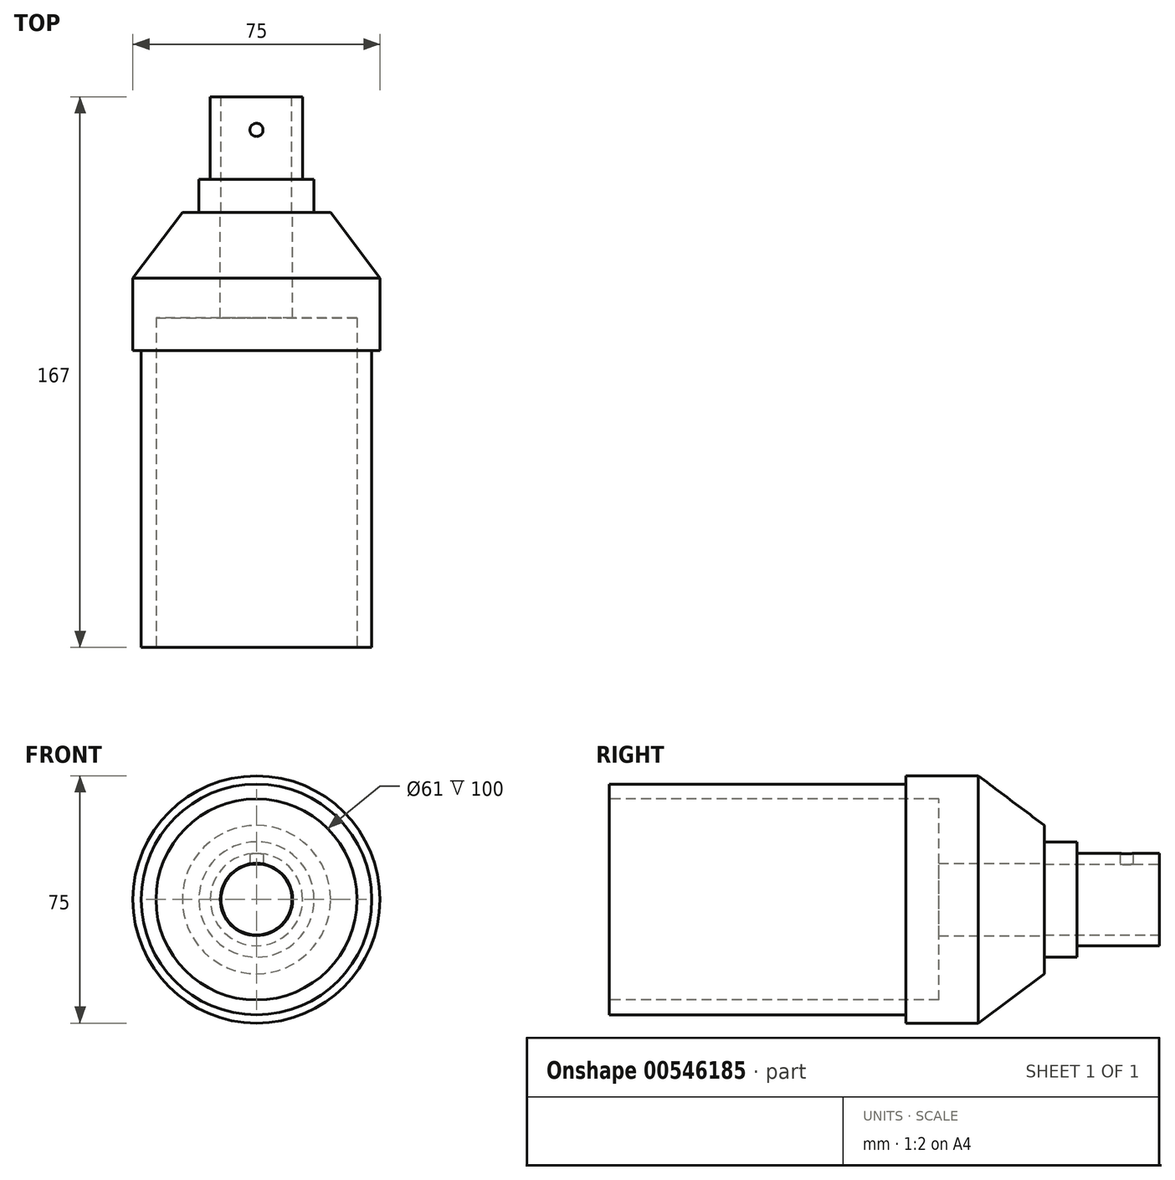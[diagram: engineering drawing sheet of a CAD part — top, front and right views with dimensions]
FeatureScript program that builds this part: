
annotation { "Feature Type Name" : "Feature", "Feature Type Description" : "" }
export const myFeature = defineFeature(function(context is Context, id is Id, definition is map)
    precondition{}
    {
        {
            var Q0;
            Q0=qCreatedBy(makeId("Front.planeOp"),FACE);
            var sketch = newSketch(context, id + "F0", { "sketchPlane" : qUnion([Q0])});
            skCircle(sketch, "E0", {"center": v(0, 0) * mm, "radius": 11 * mm});
            skCircle(sketch, "E1", {"center": v(0, 0) * mm, "radius": 37.5 * mm});
            skSolve(sketch);
        }
        {
            var Q0;
            Q0 = qSketchRegion(id + "F0", true);
            extrude(context, id + "F1", {"entities" : qUnion([Q0]), "depth" : 22 * mm, "offsetDistance" : 25 * mm});
        }
        {
            var Q0;
            Q0=makeQuery(id+"F1.opExtrude","CAP_FACE",FACE,{"disambiguationData":[OSD([sQuery(id+"F0.wireOp",EDGE,"E0"),sQuery(id+"F0.wireOp",EDGE,"E1")])],"isStart":false});
            var sketch = newSketch(context, id + "F2", { "sketchPlane" : qUnion([Q0])});
            skCircle(sketch, "E2", {"center": v(0, 0) * mm, "radius": 35 * mm});
            skSolve(sketch);
        }
        {
            var Q0;
            Q0 = qSketchRegion(id + "F2", true);
            extrude(context, id + "F3", {"entities" : qUnion([Q0]), "operationType" : NewBodyOperationType.ADD, "depth" : 90 * mm, "offsetDistance" : 25 * mm});
        }
        {
            var Q0;
            Q0=makeQuery(id+"F3.opExtrude","CAP_FACE",FACE,{"disambiguationData":[OSD([sQuery(id+"F2.wireOp",EDGE,"E2")])],"isStart":false});
            var sketch = newSketch(context, id + "F4", { "sketchPlane" : qUnion([Q0])});
            skCircle(sketch, "E3", {"center": v(0, 0) * mm, "radius": 30.5 * mm});
            skSolve(sketch);
        }
        {
            var Q0;
            Q0 = qSketchRegion(id + "F4", true);
            extrude(context, id + "F5", {"entities" : qUnion([Q0]), "operationType" : NewBodyOperationType.REMOVE, "oppositeDirection" : true, "depth" : 100 * mm, "offsetDistance" : 25 * mm});
        }
        {
            var Q0;
            Q0=makeQuery(id+"F1.opExtrude","CAP_FACE",FACE,{"disambiguationData":[OSD([sQuery(id+"F0.wireOp",EDGE,"E0"),sQuery(id+"F0.wireOp",EDGE,"E1")])],"isStart":true});
            var sketch = newSketch(context, id + "F6", { "sketchPlane" : qUnion([Q0])});
            skSolve(sketch);
        }
        {
            var Q0;
            Q0 = qSketchRegion(id + "F6", true);
            var Q1;
            Q1=makeQuery(id+"F6.imprint","IMPRINT",FACE,{"disambiguationData":[TD([[makeQuery(id+"F6.imprint","IMPRINT",EDGE,{"derivedFrom":makeQuery(id+"F1.opExtrude","CAP_EDGE",EDGE,{"disambiguationData":[OSD([sQuery(id+"F0.wireOp",EDGE,"E0")])],"isStart":true})}),1.0]])]});
            extrude(context, id + "F7", {"entities" : qUnion([Q0, Q1]), "operationType" : NewBodyOperationType.ADD, "depth" : 20 * mm, "offsetDistance" : 25 * mm});
        }
        {
            var Q0;
            Q0=makeQuery(id+"F7.opExtrude","CAP_EDGE",EDGE,{"disambiguationData":[OSD([sQuery(id+"F0.wireOp",EDGE,"E1")])],"isStart":false});
            chamfer(context, id + "F8", {"entities" : qUnion([Q0]), "chamferType" : ChamferType.TWO_OFFSETS, "width1" : 20 * mm, "oppositeDirection" : false, "width2" : 15 * mm, "tangentPropagation" : true});
        }
        {
            var Q0;
            Q0=makeQuery(id+"F7.opExtrude","CAP_FACE",FACE,{"disambiguationData":[OSD([sQuery(id+"F0.wireOp",EDGE,"E0"),sQuery(id+"F0.wireOp",EDGE,"E1")])],"isStart":false});
            var sketch = newSketch(context, id + "F9", { "sketchPlane" : qUnion([Q0])});
            skCircle(sketch, "E4", {"center": v(0, 0) * mm, "radius": 17.5 * mm});
            skSolve(sketch);
        }
        {
            var Q0;
            Q0 = qSketchRegion(id + "F9", true);
            extrude(context, id + "F10", {"entities" : qUnion([Q0]), "operationType" : NewBodyOperationType.ADD, "depth" : 10 * mm, "offsetDistance" : 25 * mm});
        }
        {
            var Q0;
            Q0=makeQuery(id+"F10.opExtrude","CAP_FACE",FACE,{"disambiguationData":[OSD([sQuery(id+"F9.wireOp",EDGE,"E4")])],"isStart":false});
            var sketch = newSketch(context, id + "F11", { "sketchPlane" : qUnion([Q0])});
            skCircle(sketch, "E5", {"center": v(0, 0) * mm, "radius": 14 * mm});
            skSolve(sketch);
        }
        {
            var Q0;
            Q0 = qSketchRegion(id + "F11", true);
            extrude(context, id + "F12", {"entities" : qUnion([Q0]), "operationType" : NewBodyOperationType.ADD, "depth" : 25 * mm, "offsetDistance" : 25 * mm});
        }
        {
            var Q0;
            Q0=makeQuery(id+"F12.opExtrude","CAP_FACE",FACE,{"disambiguationData":[OSD([sQuery(id+"F11.wireOp",EDGE,"E5")])],"isStart":false});
            var sketch = newSketch(context, id + "F13", { "sketchPlane" : qUnion([Q0])});
            skCircle(sketch, "E6", {"center": v(0, 0) * mm, "radius": 10.75 * mm});
            skSolve(sketch);
        }
        {
            var Q0;
            Q0 = qSketchRegion(id + "F13", true);
            extrude(context, id + "F14", {"entities" : qUnion([Q0]), "operationType" : NewBodyOperationType.REMOVE, "oppositeDirection" : true, "depth" : 125 * mm, "offsetDistance" : 25 * mm});
        }
        {
            var Q0;
            Q0=qCreatedBy(makeId("Top.planeOp"),FACE);
            var sketch = newSketch(context, id + "F15", { "sketchPlane" : qUnion([Q0])});
            skLineSegment(sketch, "E7", {"start": v(0, 0) * mm, "end": v(0, 45) * mm});
            skCircle(sketch, "E8", {"center": v(0, 45) * mm, "radius": 2 * mm});
            skSolve(sketch);
        }
        {
            var Q0;
            Q0 = qSketchRegion(id + "F15", true);
            extrude(context, id + "F16", {"entities" : qUnion([Q0]), "operationType" : NewBodyOperationType.REMOVE, "depth" : 25 * mm, "offsetDistance" : 25 * mm});
        }
    });
